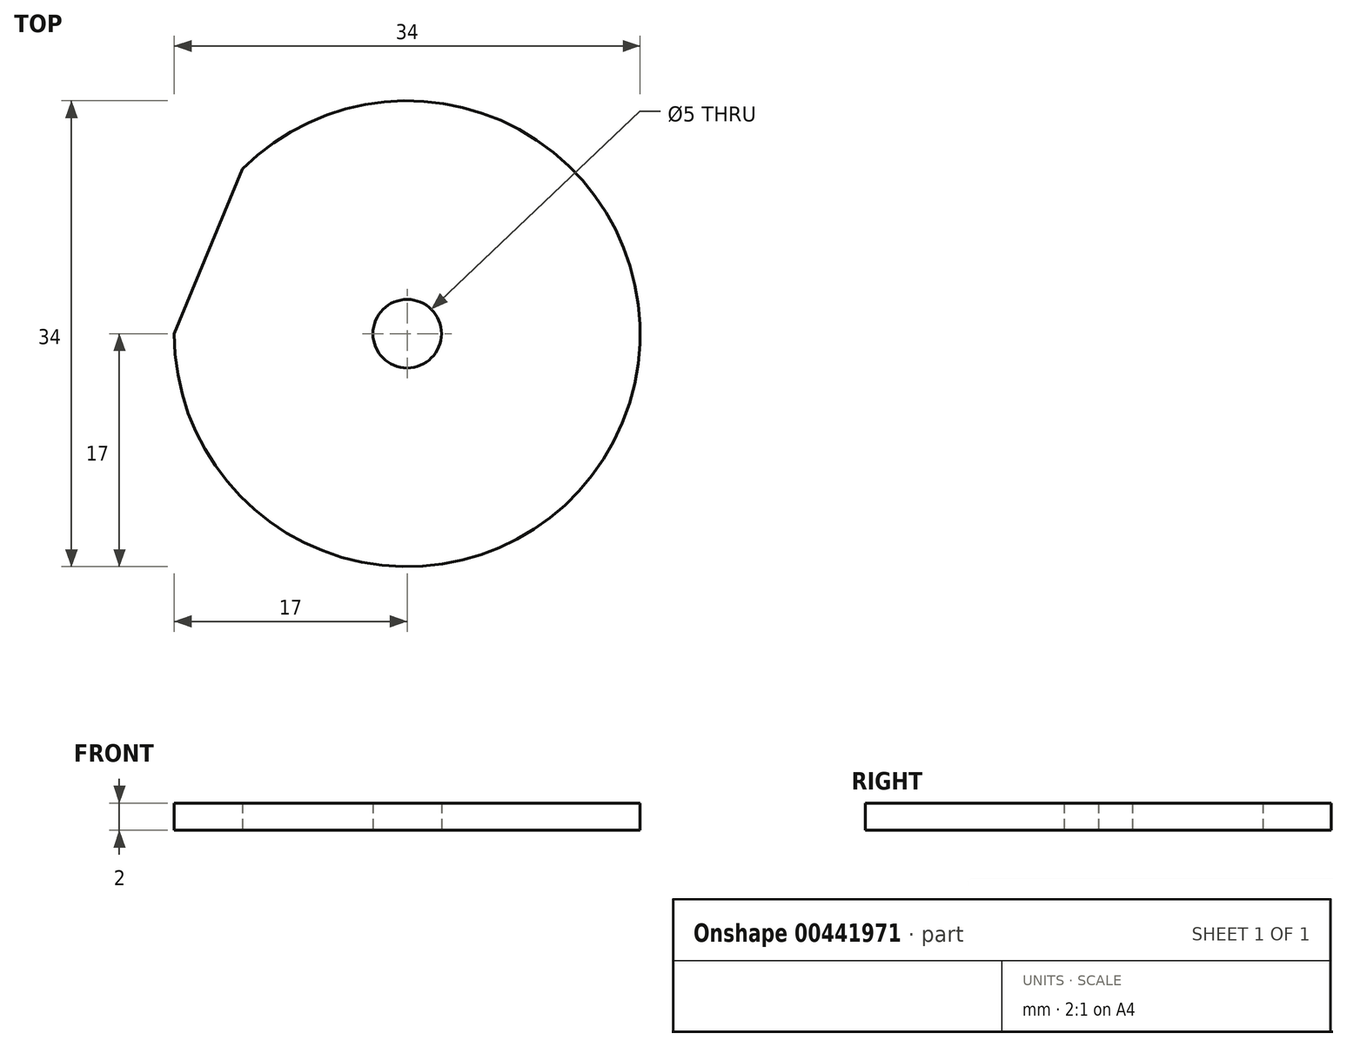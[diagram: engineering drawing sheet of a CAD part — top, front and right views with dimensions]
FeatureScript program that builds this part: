
annotation { "Feature Type Name" : "Feature", "Feature Type Description" : "" }
export const myFeature = defineFeature(function(context is Context, id is Id, definition is map)
    precondition{}
    {
        {
            var Q0;
            Q0=qCreatedBy(makeId("Top.planeOp"),FACE);
            var sketch = newSketch(context, id + "F0", { "sketchPlane" : qUnion([Q0])});
            skCircle(sketch, "E0.cCircle", {"center": v(0, 0) * mm, "radius": 17 * mm, "construction": true});
            skLineSegment(sketch, "E0.0", {"start": v(-17, 0) * mm, "end": v(-12.02, 12.02) * mm});
            skLineSegment(sketch, "E0.1", {"start": v(-12.02, 12.02) * mm, "end": v(0, 17) * mm});
            skLineSegment(sketch, "E0.2", {"start": v(0, 17) * mm, "end": v(12.02, 12.02) * mm});
            skLineSegment(sketch, "E0.3", {"start": v(12.02, 12.02) * mm, "end": v(17, 0) * mm});
            skLineSegment(sketch, "E0.4", {"start": v(17, 0) * mm, "end": v(12.02, -12.02) * mm});
            skLineSegment(sketch, "E0.5", {"start": v(12.02, -12.02) * mm, "end": v(0, -17) * mm});
            skLineSegment(sketch, "E0.6", {"start": v(0, -17) * mm, "end": v(-12.02, -12.02) * mm});
            skLineSegment(sketch, "E0.7", {"start": v(-12.02, -12.02) * mm, "end": v(-17, 0) * mm});
            skCircle(sketch, "E1", {"center": v(0, 0) * mm, "radius": 2.5 * mm});
            skPoint(sketch, "E2", {"position": v(0, 2.5) * mm});
            skCircle(sketch, "E3", {"center": v(0, 0) * mm, "radius": 17 * mm});
            skSolve(sketch);
        }
        {
            var Q0;
            Q0=makeQuery(id+"F0.imprint","IMPRINT",FACE,{"disambiguationData":[TD([[makeQuery(id+"F0.imprint","IMPRINT",EDGE,{"derivedFrom":sQuery(id+"F0.wireOp",EDGE,"E0.0")}),-1.0]])]});
            var Q1;
            {var subQ0=sQuery(id+"F0.wireOp",EDGE,"E0.7");Q1=makeQuery(id+"F0.imprint","IMPRINT",FACE,{"disambiguationData":[TD([[makeQuery(id+"F0.imprint","IMPRINT",EDGE,{"derivedFrom":subQ0}),1.0]])]});}
            var Q2;
            {var subQ0=sQuery(id+"F0.wireOp",EDGE,"E0.6");Q2=makeQuery(id+"F0.imprint","IMPRINT",FACE,{"disambiguationData":[TD([[makeQuery(id+"F0.imprint","IMPRINT",EDGE,{"derivedFrom":subQ0}),1.0]])]});}
            var Q3;
            {var subQ0=sQuery(id+"F0.wireOp",EDGE,"E0.2");Q3=makeQuery(id+"F0.imprint","IMPRINT",FACE,{"disambiguationData":[TD([[makeQuery(id+"F0.imprint","IMPRINT",EDGE,{"derivedFrom":subQ0}),1.0]])]});}
            var Q4;
            {var subQ0=sQuery(id+"F0.wireOp",EDGE,"E0.1");Q4=makeQuery(id+"F0.imprint","IMPRINT",FACE,{"disambiguationData":[TD([[makeQuery(id+"F0.imprint","IMPRINT",EDGE,{"derivedFrom":subQ0}),1.0]])]});}
            var Q5;
            {var subQ0=sQuery(id+"F0.wireOp",EDGE,"E0.5");Q5=makeQuery(id+"F0.imprint","IMPRINT",FACE,{"disambiguationData":[TD([[makeQuery(id+"F0.imprint","IMPRINT",EDGE,{"derivedFrom":subQ0}),1.0]])]});}
            var Q6;
            {var subQ0=sQuery(id+"F0.wireOp",EDGE,"E0.4");Q6=makeQuery(id+"F0.imprint","IMPRINT",FACE,{"disambiguationData":[TD([[makeQuery(id+"F0.imprint","IMPRINT",EDGE,{"derivedFrom":subQ0}),1.0]])]});}
            var Q7;
            {var subQ0=sQuery(id+"F0.wireOp",EDGE,"E0.3");Q7=makeQuery(id+"F0.imprint","IMPRINT",FACE,{"disambiguationData":[TD([[makeQuery(id+"F0.imprint","IMPRINT",EDGE,{"derivedFrom":subQ0}),1.0]])]});}
            extrude(context, id + "F1", {"entities" : qUnion([Q0, Q1, Q2, Q3, Q4, Q5, Q6, Q7]), "depth" : 2 * mm, "offsetDistance" : 25.4 * mm});
        }
    });
